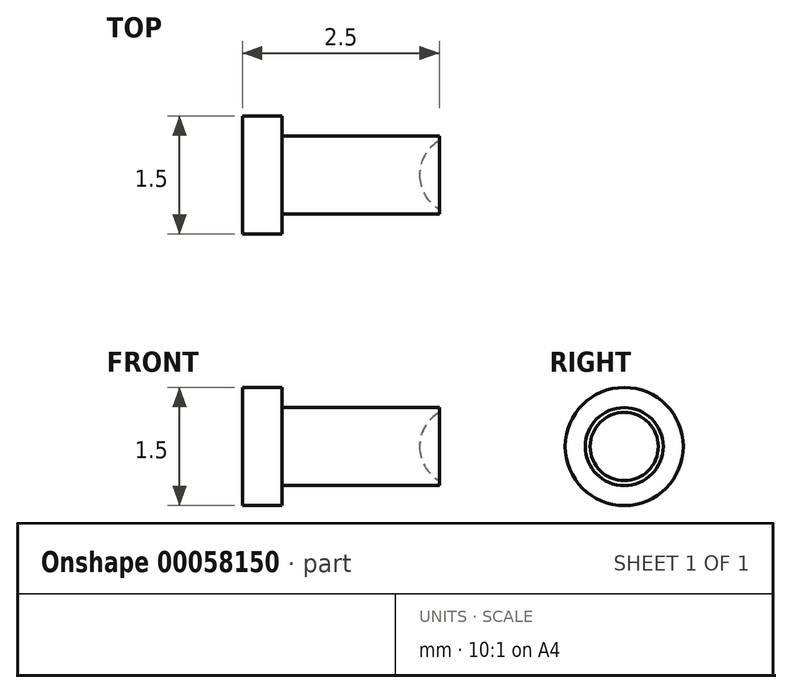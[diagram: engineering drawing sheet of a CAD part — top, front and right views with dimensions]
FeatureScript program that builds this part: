
annotation { "Feature Type Name" : "Feature", "Feature Type Description" : "" }
export const myFeature = defineFeature(function(context is Context, id is Id, definition is map)
    precondition{}
    {
        {
            var Q0;
            Q0=qCreatedBy(makeId("Front.planeOp"),FACE);
            var sketch = newSketch(context, id + "F0", { "sketchPlane" : qUnion([Q0])});
            skLineSegment(sketch, "E0", {"start": v(0, 0) * mm, "end": v(0, 0.75) * mm});
            skLineSegment(sketch, "E1", {"start": v(0, 0.75) * mm, "end": v(0.5, 0.75) * mm});
            skLineSegment(sketch, "E2", {"start": v(0.5, 0.75) * mm, "end": v(0.5, 0.5) * mm});
            skLineSegment(sketch, "E3", {"start": v(0.5, 0.5) * mm, "end": v(2.5, 0.5) * mm});
            skLineSegment(sketch, "E4", {"start": v(2.5, 0.5) * mm, "end": v(2.5, 0.43) * mm});
            skArc(sketch, "E5", {"start": v(2.5, 0.43) * mm, "mid": v(2.32, 0.25) * mm, "end": v(2.25, 0) * mm});
            skPoint(sketch, "E6.orphan", {"position": v(2.5, 0) * mm});
            skLineSegment(sketch, "E7", {"start": v(0, 0) * mm, "end": v(2.25, 0) * mm});
            skSolve(sketch);
        }
        {
            var Q0;
            Q0 = qSketchRegion(id + "F0", true);
            var Q1;
            Q1=sQuery(id+"F0.wireOp",EDGE,"E7");
            revolve(context, id + "F1", {"entities" : qUnion([Q0]), "axis" : qUnion([Q1]), "revolveType" : RevolveType.FULL});
        }
    });
